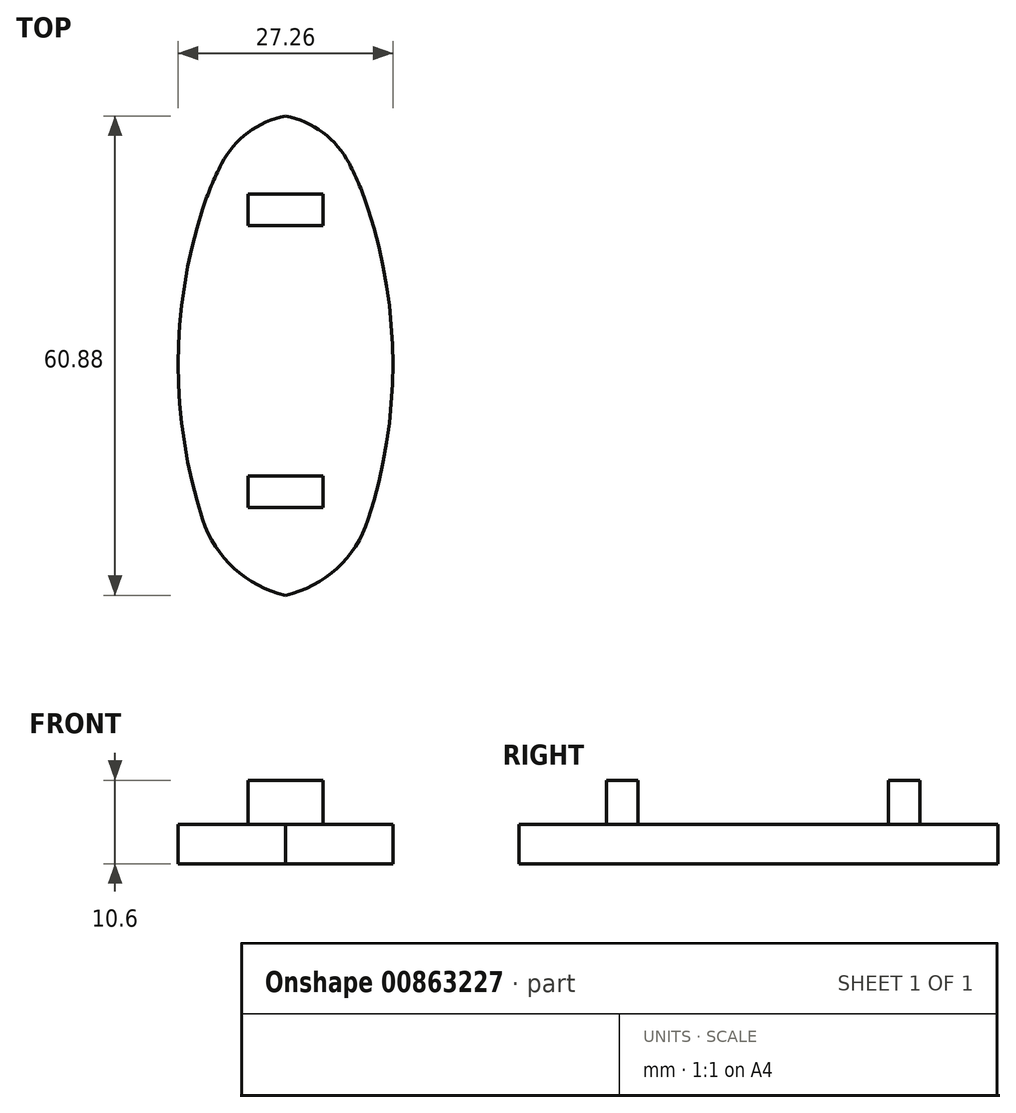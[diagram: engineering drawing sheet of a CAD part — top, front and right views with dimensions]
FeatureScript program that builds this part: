
annotation { "Feature Type Name" : "Feature", "Feature Type Description" : "" }
export const myFeature = defineFeature(function(context is Context, id is Id, definition is map)
    precondition{}
    {
        {
            var Q0;
            Q0=qCreatedBy(makeId("Top.planeOp"),FACE);
            var sketch = newSketch(context, id + "F0", { "sketchPlane" : qUnion([Q0])});
            skArc(sketch, "E0", {"start": v(8.1, 48.55) * mm, "mid": v(4.75, 52.5) * mm, "end": v(0, 54.6) * mm});
            skArc(sketch, "E1", {"start": v(10.5, 42.82) * mm, "mid": v(9.43, 45.73) * mm, "end": v(8.1, 48.55) * mm});
            skArc(sketch, "E2", {"start": v(10.5, 3.34) * mm, "mid": v(13.63, 23.08) * mm, "end": v(10.5, 42.82) * mm});
            skArc(sketch, "E3", {"start": v(0, -6.28) * mm, "mid": v(6.52, -2.85) * mm, "end": v(10.5, 3.34) * mm});
            skArc(sketch, "E4.MirrorCS", {"start": v(-8.1, 48.55) * mm, "mid": v(-4.75, 52.5) * mm, "end": v(0, 54.6) * mm});
            skArc(sketch, "E5.MirrorCS", {"start": v(-10.5, 42.82) * mm, "mid": v(-9.43, 45.73) * mm, "end": v(-8.1, 48.55) * mm});
            skArc(sketch, "E6.MirrorCS", {"start": v(-10.5, 3.34) * mm, "mid": v(-13.63, 23.08) * mm, "end": v(-10.5, 42.82) * mm});
            skArc(sketch, "E7.MirrorCS", {"start": v(0, -6.28) * mm, "mid": v(-6.52, -2.85) * mm, "end": v(-10.5, 3.34) * mm});
            skPoint(sketch, "E8.firstSnap0", {"position": v(-9.43, 45.73) * mm});
            skSolve(sketch);
        }
        {
            var Q0;
            Q0 = qSketchRegion(id + "F0", true);
            extrude(context, id + "F1", {"entities" : qUnion([Q0]), "oppositeDirection" : true, "depth" : 5 * mm, "offsetDistance" : 25 * mm});
        }
        {
            var Q0;
            Q0=qCreatedBy(makeId("Top.planeOp"),FACE);
            var sketch = newSketch(context, id + "F2", { "sketchPlane" : qUnion([Q0])});
            skLineSegment(sketch, "E9.bottom", {"start": v(0, 8.87) * mm, "end": v(-4.75, 8.87) * mm});
            skLineSegment(sketch, "E9.top", {"start": v(0, 4.87) * mm, "end": v(-4.75, 4.87) * mm});
            skLineSegment(sketch, "E9.right", {"start": v(-4.75, 8.87) * mm, "end": v(-4.75, 4.87) * mm});
            skLineSegment(sketch, "E10.bottom", {"start": v(0, 44.7) * mm, "end": v(-4.75, 44.7) * mm});
            skLineSegment(sketch, "E10.top", {"start": v(0, 40.7) * mm, "end": v(-4.75, 40.7) * mm});
            skLineSegment(sketch, "E10.right", {"start": v(-4.75, 44.7) * mm, "end": v(-4.75, 40.7) * mm});
            skLineSegment(sketch, "E11.MirrorCS", {"start": v(0, 44.7) * mm, "end": v(4.75, 44.7) * mm});
            skLineSegment(sketch, "E12.MirrorCS", {"start": v(0, 40.7) * mm, "end": v(4.75, 40.7) * mm});
            skLineSegment(sketch, "E13.MirrorCS", {"start": v(4.75, 44.7) * mm, "end": v(4.75, 40.7) * mm});
            skLineSegment(sketch, "E14.MirrorCS", {"start": v(0, 8.87) * mm, "end": v(4.75, 8.87) * mm});
            skLineSegment(sketch, "E15.MirrorCS", {"start": v(4.75, 8.87) * mm, "end": v(4.75, 4.87) * mm});
            skLineSegment(sketch, "E16.MirrorCS", {"start": v(0, 4.87) * mm, "end": v(4.75, 4.87) * mm});
            skSolve(sketch);
        }
        {
            var Q0;
            Q0 = qSketchRegion(id + "F2", true);
            extrude(context, id + "F3", {"entities" : qUnion([Q0]), "operationType" : NewBodyOperationType.ADD, "depth" : 5.6 * mm, "offsetDistance" : 25 * mm});
        }
    });
